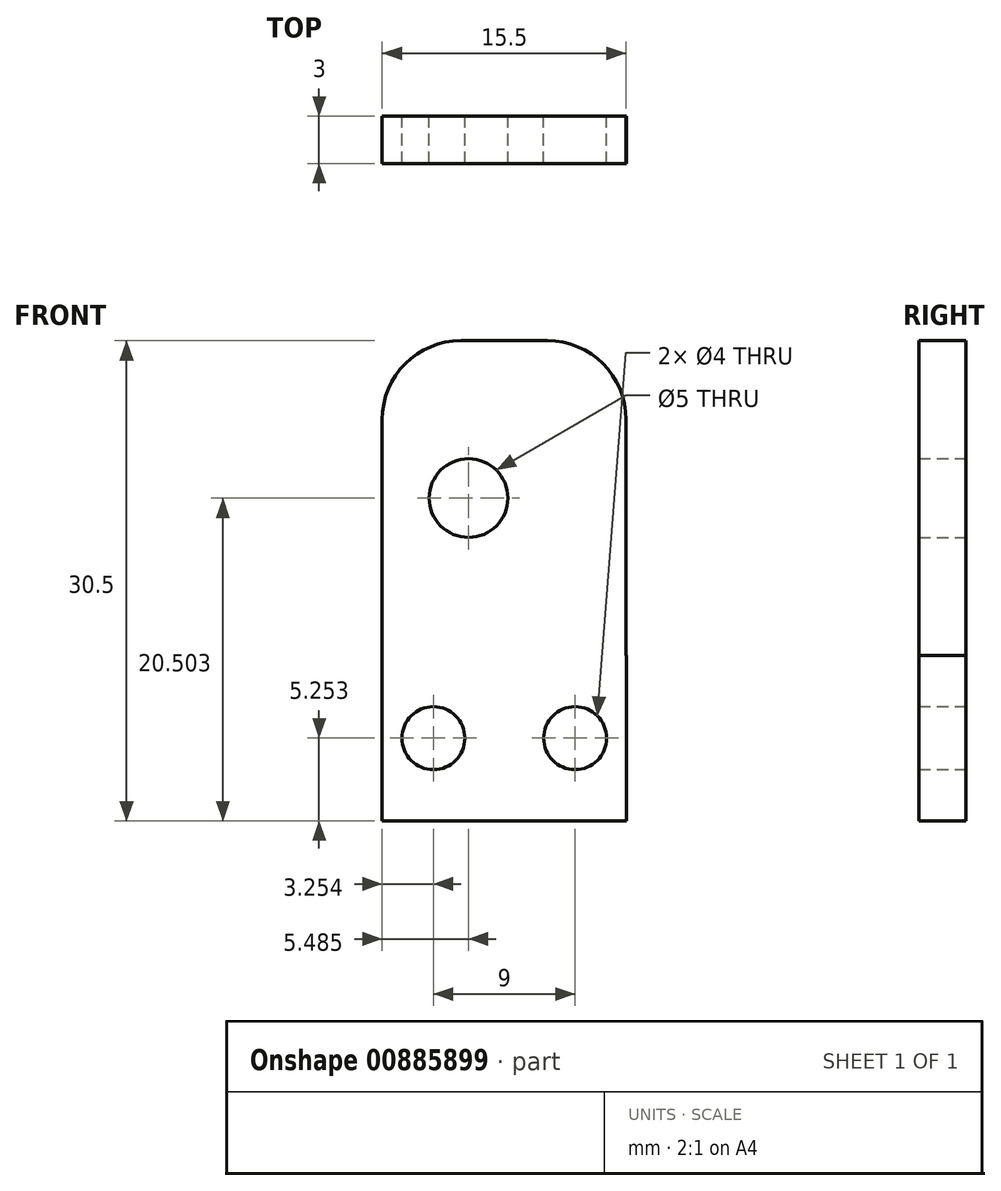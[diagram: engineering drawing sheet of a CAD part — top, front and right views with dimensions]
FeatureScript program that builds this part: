
annotation { "Feature Type Name" : "Feature", "Feature Type Description" : "" }
export const myFeature = defineFeature(function(context is Context, id is Id, definition is map)
    precondition{}
    {
        {
            var Q0;
            Q0=qCreatedBy(makeId("Front.planeOp"),FACE);
            var sketch = newSketch(context, id + "F0", { "sketchPlane" : qUnion([Q0])});
            skPoint(sketch, "E0.visualSharp", {"position": v(-41.95, 48.12) * mm});
            skLineSegment(sketch, "E1.0", {"start": v(-26.7, 48.35) * mm, "end": v(-26.7, 37.85) * mm});
            skLineSegment(sketch, "E1.1", {"start": v(-36.54, 48.35) * mm, "end": v(-26.7, 48.35) * mm});
            skLineSegment(sketch, "E1.2", {"start": v(-42.2, 37.85) * mm, "end": v(-26.7, 37.85) * mm});
            skLineSegment(sketch, "E1.3", {"start": v(-42.2, 43.12) * mm, "end": v(-42.2, 37.85) * mm});
            skArc(sketch, "E1.4", {"start": v(-36.54, 48.35) * mm, "mid": v(-40.51, 46.97) * mm, "end": v(-42.2, 43.12) * mm});
            skCircle(sketch, "E2", {"center": v(-29.95, 43.1) * mm, "radius": 2 * mm});
            skCircle(sketch, "E3", {"center": v(-38.95, 43.1) * mm, "radius": 2 * mm});
            skLineSegment(sketch, "E4.bottom", {"start": v(-37.2, 68.35) * mm, "end": v(-31.71, 68.35) * mm});
            skLineSegment(sketch, "E4.top", {"start": v(-42.2, 37.85) * mm, "end": v(-26.71, 37.85) * mm});
            skLineSegment(sketch, "E4.left", {"start": v(-42.2, 63.35) * mm, "end": v(-42.2, 37.85) * mm});
            skLineSegment(sketch, "E4.right", {"start": v(-26.71, 63.35) * mm, "end": v(-26.71, 37.85) * mm});
            skPoint(sketch, "E5.visualSharp", {"position": v(-42.2, 68.35) * mm});
            skArc(sketch, "E5.filletArc", {"start": v(-37.2, 68.35) * mm, "mid": v(-40.73, 66.89) * mm, "end": v(-42.2, 63.35) * mm});
            skPoint(sketch, "E6.visualSharp", {"position": v(-26.71, 68.35) * mm});
            skArc(sketch, "E6.filletArc", {"start": v(-26.71, 63.35) * mm, "mid": v(-28.18, 66.89) * mm, "end": v(-31.71, 68.35) * mm});
            skCircle(sketch, "E7", {"center": v(-36.71, 58.35) * mm, "radius": 2.5 * mm});
            skSolve(sketch);
        }
        {
            var Q0;
            Q0 = qSketchRegion(id + "F0", true);
            extrude(context, id + "F1", {"entities" : qUnion([Q0]), "depth" : 3 * mm, "offsetDistance" : 25 * mm});
        }
    });
